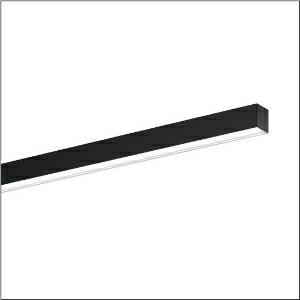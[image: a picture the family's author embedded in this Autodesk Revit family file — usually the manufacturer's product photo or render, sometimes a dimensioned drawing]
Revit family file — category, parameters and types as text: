
# Revit family: silica_21_51mx20tat2b
name_source: partatom
category: Lighting Fixtures
units: mm (PartAtom-declared; Revit-internal decimal feet)

## family parameters
Cut with Voids When Loaded = No
Host = Face
Light Source = No
Part Type = Normal
Room Calculation Point = No
Round Connector Dimension = Use Diameter
Shared = No

## types (1)
- --- (1 x LED, 2400 lm, 20.5 W, 6500K)
    Apparent Load = 21 VA
    CIE Flux Codes = 48 79 96 100 100
    Color Rendering = 80
    Color Temperature = 6500K
    Default Elevation = 1800 mm
    Description = Silica 21, office luminaire, primary optical cover: cover, of PMMA, opal, light emission: direct distribution, primary light characteristic: symmetric, installation type: surface-mounted, LED, rated luminous flux: 2.400lm, luminous efficacy: 112lm/W, light colour: 8tw, colour temperature: 2700..6500K, control gear: DALI DT8, with terminal, 3+2-pole, max. 2.5mm², mains connection: 220..240V, AC, 50/60Hz, rated input power: 21.5W, luminaire housing, of aluminium, matt jet black (RAL 9005), length: 1.204mm, width: 53mm, height: 53mm, protection rating (complete): IP20, insulation class (complete): insulation class I (protective earthing), certification: CE, permissible operating ambient temperature: 0..+35°C, standard: EN 50419, packaging unit: 1 piece
    Height = 53 mm
    Lamp = 1 x LED
    Lamp Light Flux = 2400 lm
    Lamp Power = 20.5 W
    Lamp count = 1
    Length = 1204 mm
    Luminous efficacy = 117 lm/W
    Manufacturer = Siteco
    ModVariant = No
    Model = 51MX20TAT2B
    Mounting Place = Ceiling
    Mounting Type = Surface mounted
    Number of Poles = 1
    OnlyDefault = Yes
    Power Factor = 1
    Product Name = Silica 21
    Product group = office luminaire | ceiling mounted
    ProductGroupID = 301
    Protection Class = Protection class I
    Protection Degree = IP 20
    RLX_Detail_Level = 1
    RLX_Emergency_Light_Flux = 0 lm
    RLX_Emergency_Type = 0
    RLX_Emergency_Type_DB = No
    RlxData = <blob elided: 25617 chars, md5=3d0045fd>
    Socket = socket
    Standby Power = 0 W
    System Light Flux = 2400 lm
    System Power = 21 W
    Type Comments = individual setting
    Type Image = l_1335925.jpg
    URL = http://relux.com
    VarID = @adj_139187
    Voltage = 0 V
    Weight = 0.00 kg
    Width = 53 mm

## geometry (parser evidence)
native form markers: Blend x4, Sweep x10
no freeform markers — native parametric forms only
